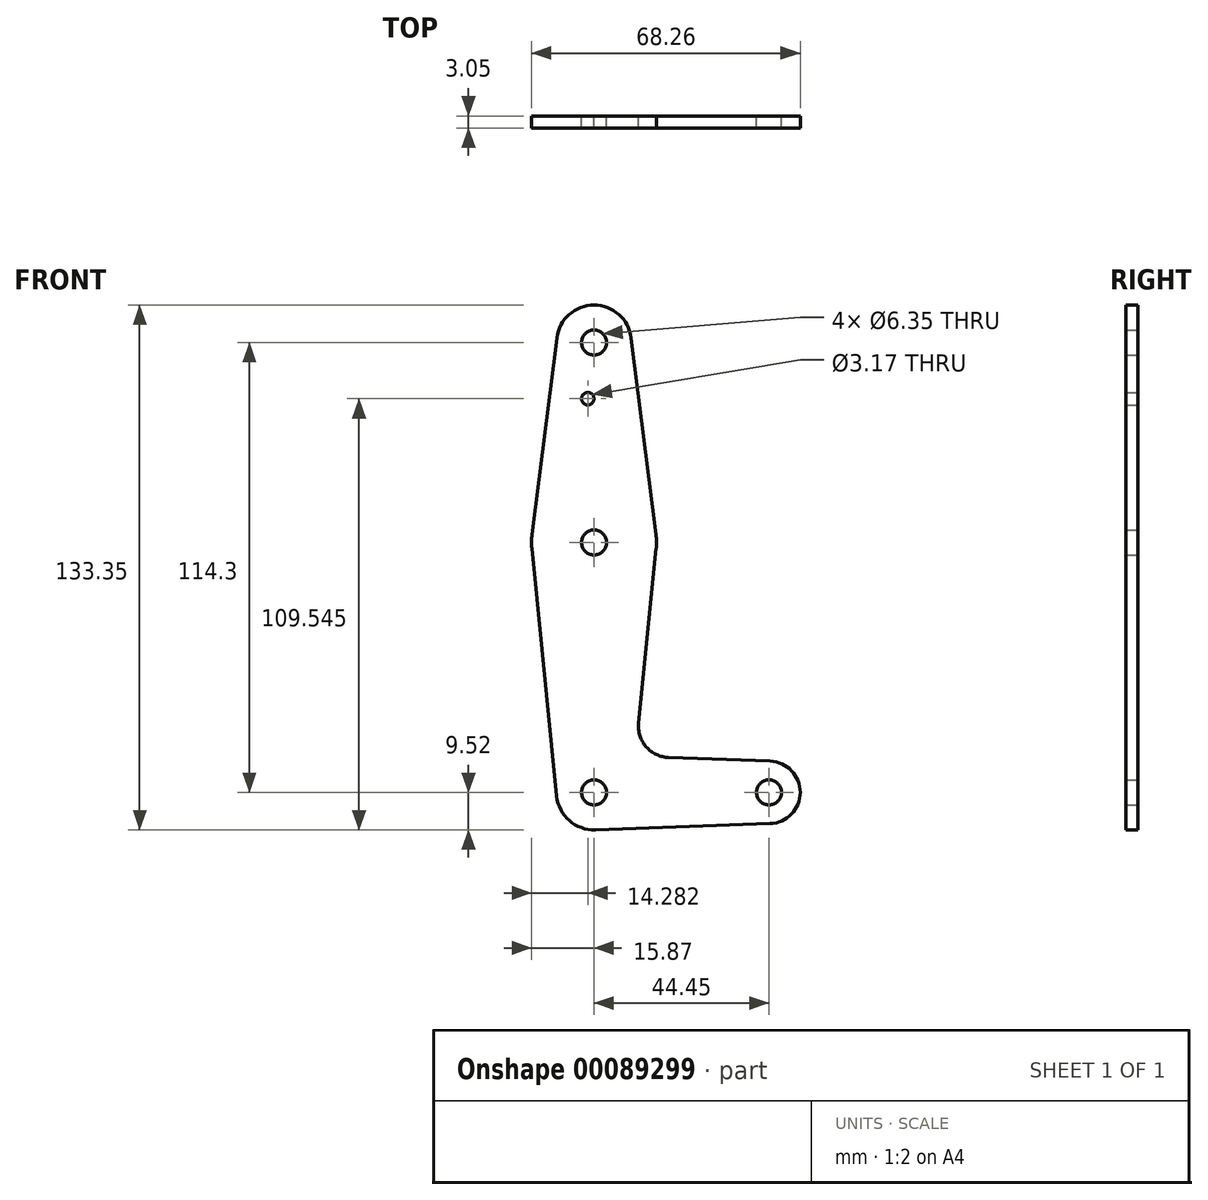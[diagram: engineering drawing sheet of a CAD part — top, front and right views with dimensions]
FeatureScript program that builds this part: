
annotation { "Feature Type Name" : "Feature", "Feature Type Description" : "" }
export const myFeature = defineFeature(function(context is Context, id is Id, definition is map)
    precondition{}
    {
        {
            var Q0;
            Q0=qCreatedBy(makeId("Front.planeOp"),FACE);
            var sketch = newSketch(context, id + "F0", { "sketchPlane" : qUnion([Q0])});
            skCircle(sketch, "E0", {"center": v(0, 0) * mm, "radius": 9.53 * mm});
            skCircle(sketch, "E1", {"center": v(0, 63.5) * mm, "radius": 15.88 * mm});
            skCircle(sketch, "E2", {"center": v(0, 114.3) * mm, "radius": 9.53 * mm});
            skCircle(sketch, "E3", {"center": v(44.45, 0) * mm, "radius": 7.94 * mm});
            skLineSegment(sketch, "E4", {"start": v(0, 114.3) * mm, "end": v(0, 63.5) * mm, "construction": true});
            skLineSegment(sketch, "E5", {"start": v(0, 63.5) * mm, "end": v(0, 0) * mm, "construction": true});
            skLineSegment(sketch, "E6", {"start": v(0, 0) * mm, "end": v(44.45, 0) * mm});
            skLineSegment(sketch, "E7", {"start": v(15.8, 61.91) * mm, "end": v(11.34, 17.6) * mm});
            skLineSegment(sketch, "E8", {"start": v(-9.45, 115.5) * mm, "end": v(-15.75, 65.48) * mm});
            skLineSegment(sketch, "E9", {"start": v(9.45, 115.5) * mm, "end": v(15.75, 65.48) * mm});
            skCircle(sketch, "E10", {"center": v(-1.59, 100.03) * mm, "radius": 1.59 * mm});
            skLineSegment(sketch, "E11", {"start": v(44.73, 7.93) * mm, "end": v(18.97, 8.85) * mm});
            skLineSegment(sketch, "E12", {"start": v(0.34, -9.52) * mm, "end": v(44.73, -7.93) * mm});
            skLineSegment(sketch, "E13", {"start": v(-15.8, 61.91) * mm, "end": v(-9.48, -0.95) * mm});
            skPoint(sketch, "E14.newPointA", {"position": v(9.57, 0) * mm});
            skArc(sketch, "E14.filletArc", {"start": v(11.34, 17.6) * mm, "mid": v(13.26, 11.57) * mm, "end": v(18.97, 8.85) * mm});
            skCircle(sketch, "E15", {"center": v(0, 114.3) * mm, "radius": 3.18 * mm});
            skCircle(sketch, "E16", {"center": v(0, 63.5) * mm, "radius": 3.18 * mm});
            skCircle(sketch, "E17", {"center": v(0, 0) * mm, "radius": 3.18 * mm});
            skCircle(sketch, "E18", {"center": v(44.45, 0) * mm, "radius": 3.18 * mm});
            skSolve(sketch);
        }
        {
            var Q0;
            Q0=makeQuery(id+"F0.imprint","IMPRINT",FACE,{"disambiguationData":[TD([[makeQuery(id+"F0.imprint","IMPRINT",EDGE,{"derivedFrom":sQuery(id+"F0.wireOp",EDGE,"E15")}),-1.0]])]});
            var Q1;
            {var subQ1=sQuery(id+"F0.wireOp",EDGE,"E8");Q1=makeQuery(id+"F0.imprint","IMPRINT",FACE,{"disambiguationData":[TD([[makeQuery(id+"F0.imprint","IMPRINT",EDGE,{"derivedFrom":subQ1}),1.0]])]});}
            var Q2;
            Q2=makeQuery(id+"F0.imprint","IMPRINT",FACE,{"disambiguationData":[TD([[makeQuery(id+"F0.imprint","IMPRINT",EDGE,{"derivedFrom":sQuery(id+"F0.wireOp",EDGE,"E16")}),-1.0]])]});
            var Q3;
            Q3=makeQuery(id+"F0.imprint","IMPRINT",FACE,{"disambiguationData":[TD([[makeQuery(id+"F0.imprint","IMPRINT",EDGE,{"derivedFrom":sQuery(id+"F0.wireOp",EDGE,"E17")}),-1.0]])]});
            var Q4;
            {var subQ0=sQuery(id+"F0.wireOp",EDGE,"E12");Q4=makeQuery(id+"F0.imprint","IMPRINT",FACE,{"disambiguationData":[TD([[makeQuery(id+"F0.imprint","IMPRINT",EDGE,{"derivedFrom":subQ0}),1.0]])]});}
            var Q5;
            Q5=makeQuery(id+"F0.imprint","IMPRINT",FACE,{"disambiguationData":[TD([[makeQuery(id+"F0.imprint","IMPRINT",EDGE,{"derivedFrom":sQuery(id+"F0.wireOp",EDGE,"E18")}),-1.0]])]});
            var Q6;
            {var subQ5=sQuery(id+"F0.wireOp",EDGE,"E7");Q6=makeQuery(id+"F0.imprint","IMPRINT",FACE,{"disambiguationData":[TD([[makeQuery(id+"F0.imprint","IMPRINT",EDGE,{"derivedFrom":subQ5}),-1.0]])]});}
            extrude(context, id + "F1", {"entities" : qUnion([Q0, Q1, Q2, Q3, Q4, Q5, Q6]), "depth" : 3.05 * mm});
        }
    });
